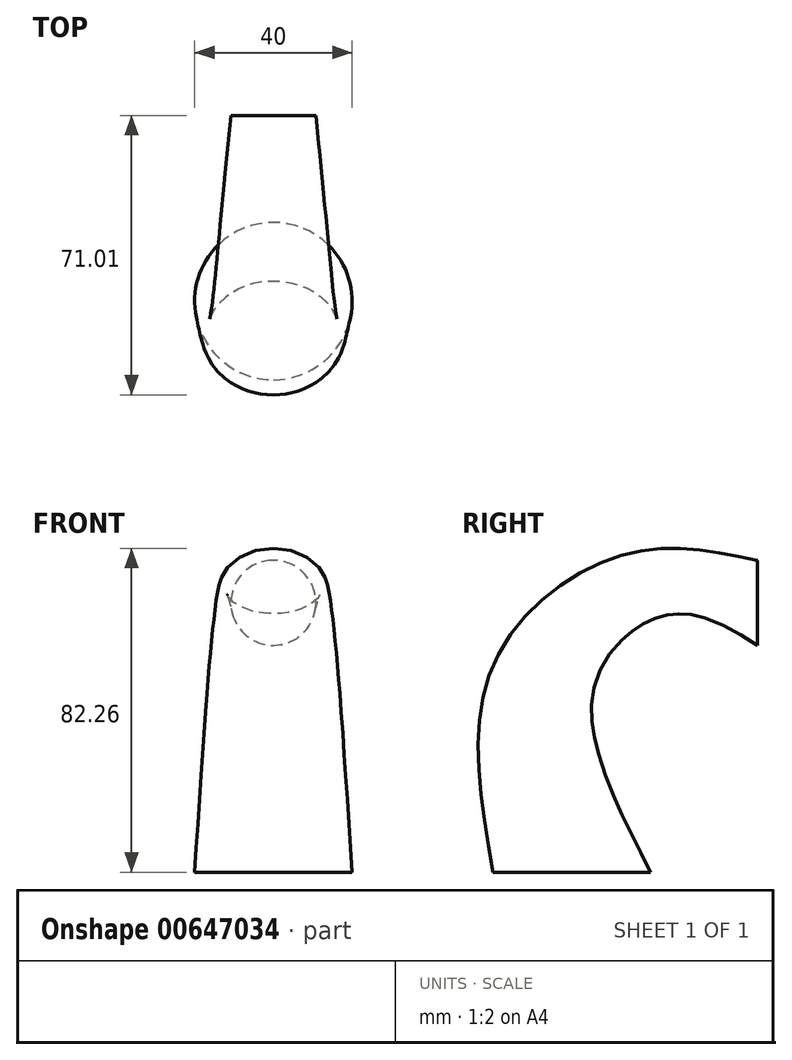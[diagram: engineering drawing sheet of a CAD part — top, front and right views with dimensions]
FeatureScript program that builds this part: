
annotation { "Feature Type Name" : "Feature", "Feature Type Description" : "" }
export const myFeature = defineFeature(function(context is Context, id is Id, definition is map)
    precondition{}
    {
        {
            var Q0;
            Q0=qCreatedBy(makeId("Top.planeOp"),FACE);
            var sketch = newSketch(context, id + "F0", { "sketchPlane" : qUnion([Q0])});
            skCircle(sketch, "E0", {"center": v(0, 0) * mm, "radius": 20 * mm});
            skSolve(sketch);
        }
        {
            var Q0;
            Q0=qCreatedBy(makeId("Right.planeOp"),FACE);
            var sketch = newSketch(context, id + "F1", { "sketchPlane" : qUnion([Q0])});
            skLineSegment(sketch, "E1.0", {"start": v(-20, 0) * mm, "end": v(20, 0) * mm, "construction": true});
            skLineSegment(sketch, "E2", {"start": v(47.21, 79.22) * mm, "end": v(47.21, 0) * mm, "construction": true});
            skLineSegment(sketch, "E3", {"start": v(20, 0) * mm, "end": v(47.21, 57.63) * mm});
            skFitSpline(sketch, "E4", {"points": [v(-20, 0) * mm, v(-20, 52.57) * mm, v(13.55, 80.72) * mm, v(47.21, 79.22) * mm], "startDerivative": vector(-26.77, 152.5) * mm, "endDerivative": vector(111.75, -23.74) * mm});
            skLineSegment(sketch, "E5", {"start": v(-20, 0) * mm, "end": v(-20, 69.63) * mm, "construction": true});
            skSolve(sketch);
        }
        {
            var Q0;
            Q0=sQuery(id+"F1.wireOp",EDGE,"E2");
            cPlane(context, id + "F2", {"entities" : qUnion([Q0]), "cplaneType" : CPlaneType.LINE_ANGLE, "offset" : 0 * mm, "angle" : 90 * degree, "width" : 150 * mm, "height" : 150 * mm});
        }
        {
            var Q0;
            Q0=qCreatedBy(id+"F2.planeOp",FACE);
            var sketch = newSketch(context, id + "F3", { "sketchPlane" : qUnion([Q0])});
            skCircle(sketch, "E6", {"center": v(0, 68.42) * mm, "radius": 10.8 * mm});
            skSolve(sketch);
        }
        {
            var Q0;
            Q0=makeQuery(id+"F3.imprint","IMPRINT",FACE,{"disambiguationData":[TD([[makeQuery(id+"F3.imprint","IMPRINT",EDGE,{"derivedFrom":sQuery(id+"F3.wireOp",EDGE,"E6")}),1.0]])]});
            var Q1;
            Q1=makeQuery(id+"F0.imprint","IMPRINT",FACE,{"disambiguationData":[TD([[makeQuery(id+"F0.imprint","IMPRINT",EDGE,{"derivedFrom":sQuery(id+"F0.wireOp",EDGE,"E0")}),1.0]])]});
            var Q2;
            Q2=sQuery(id+"F1.wireOp",EDGE,"E4");
            loft(context, id + "F4", {"addGuides" : true, "sheetProfilesArray" : [{ "sheetProfileEntities" : qUnion([Q0]) }, { "sheetProfileEntities" : qUnion([Q1]) }], "guidesArray" : [{ "guideEntities" : qUnion([Q2]), "guideDerivativeType" : LoftGuideDerivativeType.DEFAULT, "guideDerivativeMagnitude" : 1 }]});
        }
    });
